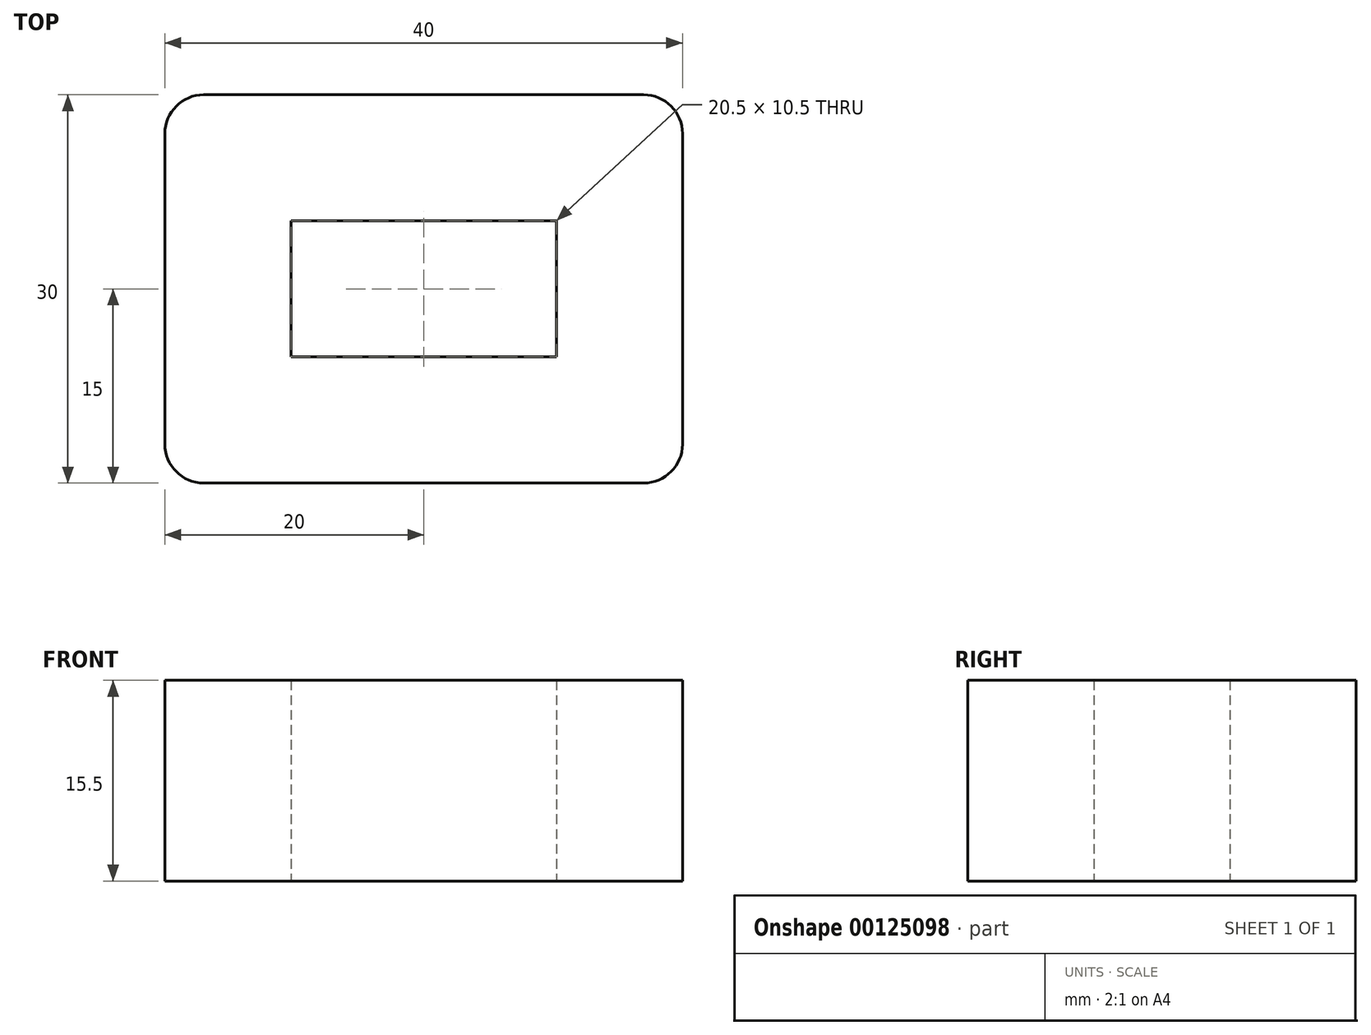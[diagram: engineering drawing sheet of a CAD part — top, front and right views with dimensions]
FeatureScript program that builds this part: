
annotation { "Feature Type Name" : "Feature", "Feature Type Description" : "" }
export const myFeature = defineFeature(function(context is Context, id is Id, definition is map)
    precondition{}
    {
        {
            var Q0;
            Q0=qCreatedBy(makeId("Top.planeOp"),FACE);
            var sketch = newSketch(context, id + "F0", { "sketchPlane" : qUnion([Q0])});
            skLineSegment(sketch, "E0.bottom", {"start": v(20, 15) * mm, "end": v(-20, 15) * mm});
            skLineSegment(sketch, "E0.top", {"start": v(20, -15) * mm, "end": v(-20, -15) * mm});
            skLineSegment(sketch, "E0.left", {"start": v(20, 15) * mm, "end": v(20, -15) * mm});
            skLineSegment(sketch, "E0.right", {"start": v(-20, 15) * mm, "end": v(-20, -15) * mm});
            skPoint(sketch, "E0.middle", {"position": v(0, 0) * mm});
            skLineSegment(sketch, "E1.bottom", {"start": v(10.25, 5.25) * mm, "end": v(-10.25, 5.25) * mm});
            skLineSegment(sketch, "E1.top", {"start": v(10.25, -5.25) * mm, "end": v(-10.25, -5.25) * mm});
            skLineSegment(sketch, "E1.left", {"start": v(10.25, 5.25) * mm, "end": v(10.25, -5.25) * mm});
            skLineSegment(sketch, "E1.right", {"start": v(-10.25, 5.25) * mm, "end": v(-10.25, -5.25) * mm});
            skSolve(sketch);
        }
        {
            var Q0;
            Q0 = qSketchRegion(id + "F0", true);
            extrude(context, id + "F1", {"entities" : qUnion([Q0]), "depth" : 15.5 * mm});
        }
        {
            var Q0;
            Q0=makeQuery(id+"F1.opExtrude","SWEPT_EDGE",EDGE,{"disambiguationData":[OSD([sQuery(id+"F0.wireOp",EDGE,"E0.bottom"),sQuery(id+"F0.wireOp",EDGE,"E0.right")])]});
            var Q1;
            Q1=makeQuery(id+"F1.opExtrude","SWEPT_EDGE",EDGE,{"disambiguationData":[OSD([sQuery(id+"F0.wireOp",EDGE,"E0.top"),sQuery(id+"F0.wireOp",EDGE,"E0.right")])]});
            var Q2;
            Q2=makeQuery(id+"F1.opExtrude","SWEPT_EDGE",EDGE,{"disambiguationData":[OSD([sQuery(id+"F0.wireOp",EDGE,"E0.top"),sQuery(id+"F0.wireOp",EDGE,"E0.left")])]});
            var Q3;
            Q3=makeQuery(id+"F1.opExtrude","SWEPT_EDGE",EDGE,{"disambiguationData":[OSD([sQuery(id+"F0.wireOp",EDGE,"E0.bottom"),sQuery(id+"F0.wireOp",EDGE,"E0.left")])]});
            fillet(context, id + "F2", {"entities" : qUnion([Q0, Q1, Q2, Q3]), "radius" : 3 * mm, "tangentPropagation" : true, "allowEdgeOverflow" : false});
        }
    });
